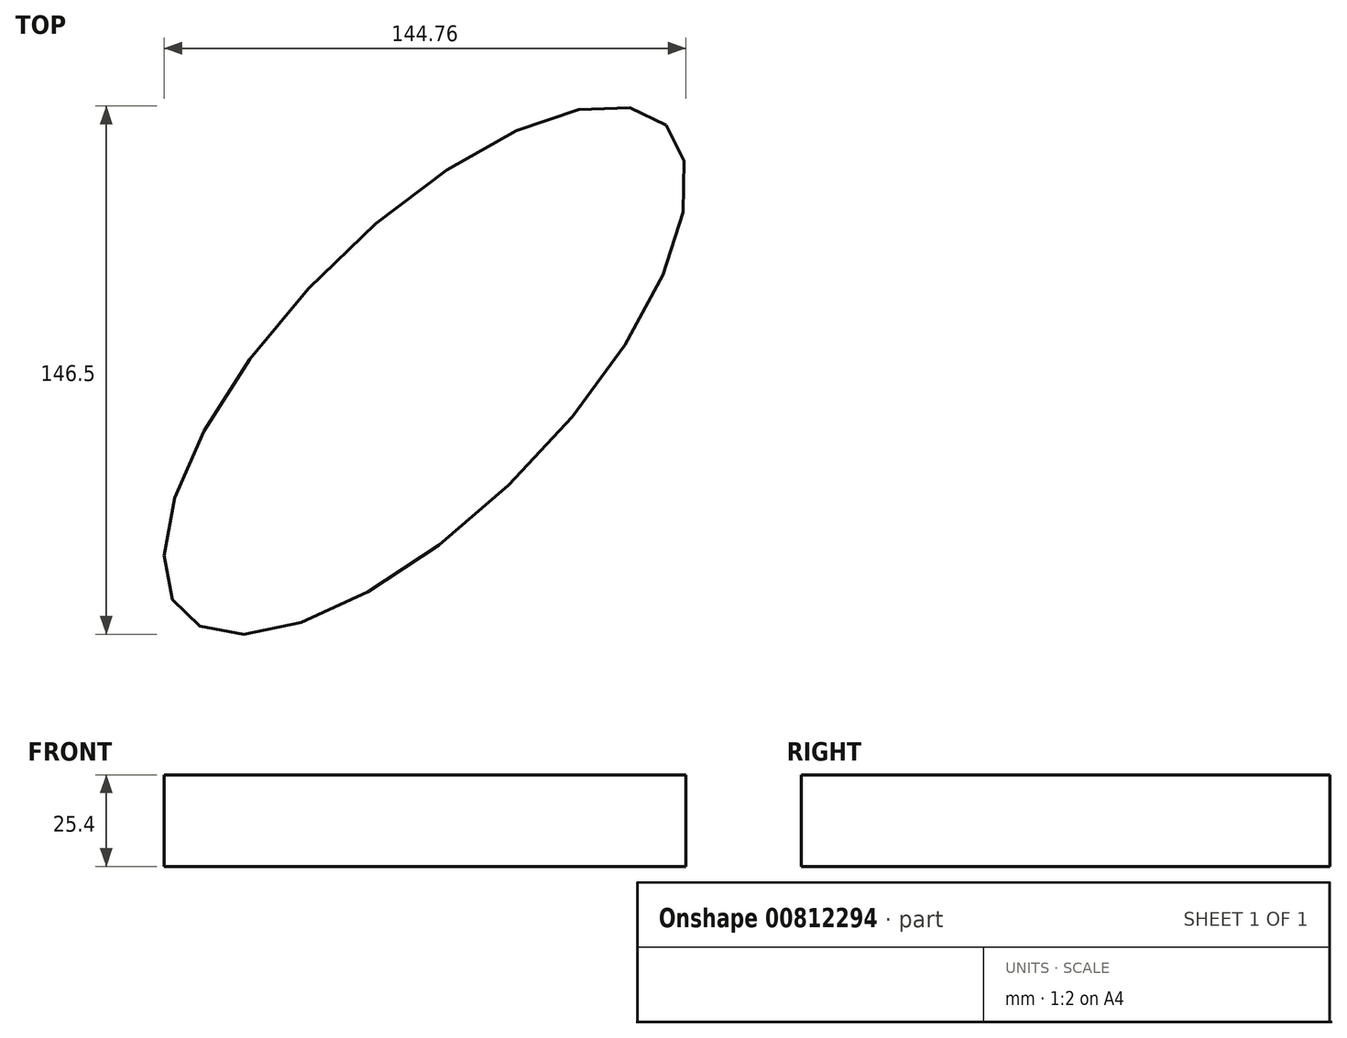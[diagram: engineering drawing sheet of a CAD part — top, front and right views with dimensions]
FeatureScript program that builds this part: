
annotation { "Feature Type Name" : "Feature", "Feature Type Description" : "" }
export const myFeature = defineFeature(function(context is Context, id is Id, definition is map)
    precondition{}
    {
        {
            var Q0;
            Q0=qCreatedBy(makeId("Top.planeOp"),FACE);
            var sketch = newSketch(context, id + "F0", { "sketchPlane" : qUnion([Q0])});
            skEllipse(sketch, "E0", {"center": v(0, 0) * mm, "majorRadius": 95.31 * mm, "minorRadius": 38.99 * mm, "majorAxis": v(0.7, 0.71)});
            skSolve(sketch);
        }
        {
            var Q0;
            Q0=makeQuery(id+"F0.imprint","IMPRINT",FACE,{"disambiguationData":[TD([[makeQuery(id+"F0.imprint","IMPRINT",EDGE,{"derivedFrom":sQuery(id+"F0.wireOp",EDGE,"E0")}),1.0]])]});
            extrude(context, id + "F1", {"entities" : qUnion([Q0]), "depth" : 25.4 * mm, "offsetDistance" : 25.4 * mm});
        }
    });
